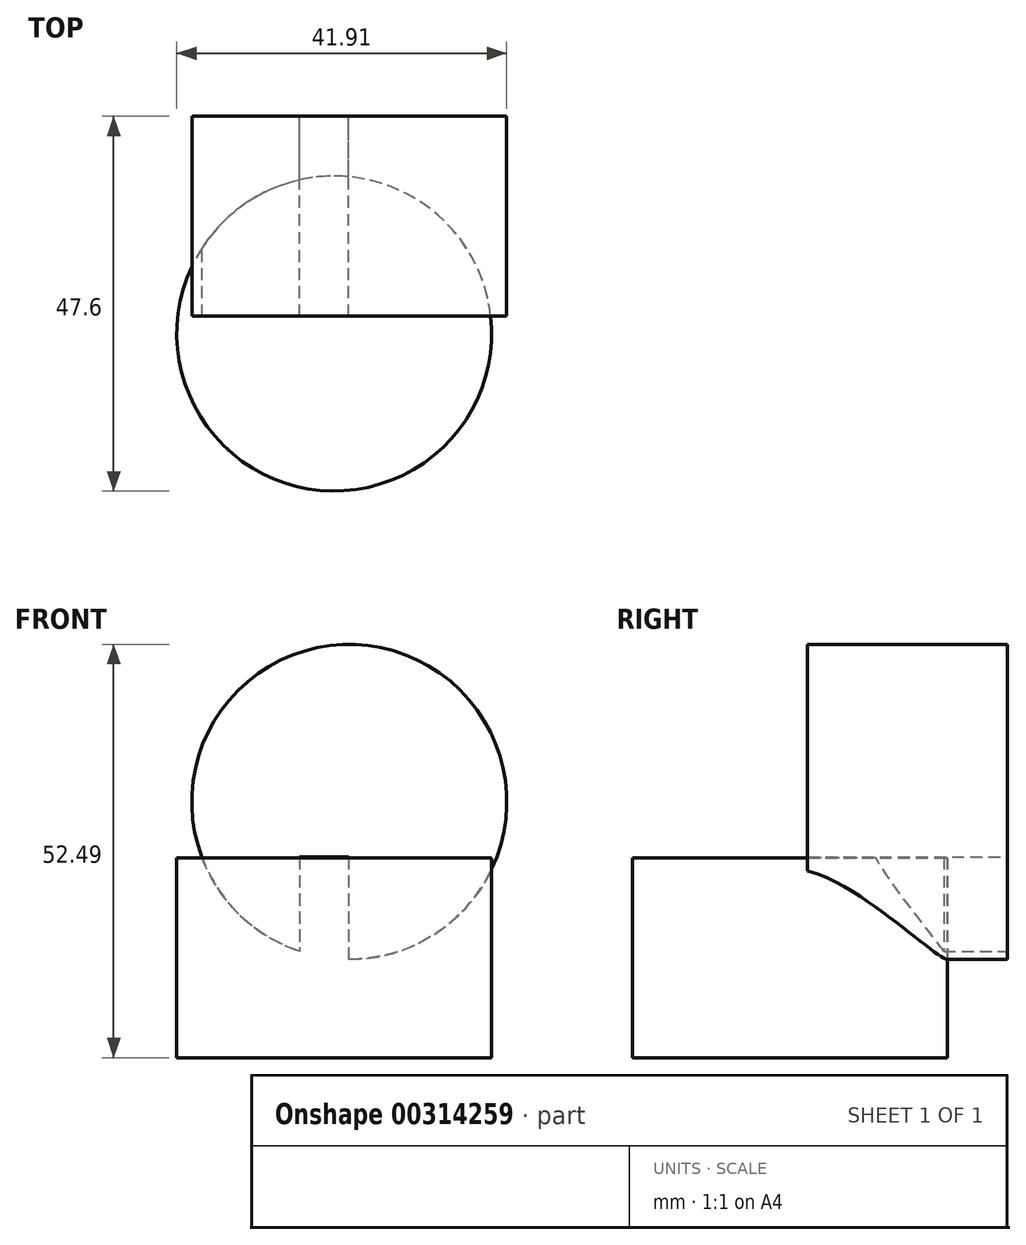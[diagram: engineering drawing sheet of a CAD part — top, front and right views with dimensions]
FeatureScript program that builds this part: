
annotation { "Feature Type Name" : "Feature", "Feature Type Description" : "" }
export const myFeature = defineFeature(function(context is Context, id is Id, definition is map)
    precondition{}
    {
        {
            var Q0;
            Q0=qCreatedBy(makeId("Top.planeOp"),FACE);
            var sketch = newSketch(context, id + "F0", { "sketchPlane" : qUnion([Q0])});
            skCircle(sketch, "E0", {"center": v(27.24, -27.6) * mm, "radius": 20 * mm});
            skSolve(sketch);
        }
        {
            var Q0;
            Q0 = qSketchRegion(id + "F0", true);
            extrude(context, id + "F1", {"entities" : qUnion([Q0]), "depth" : 25.4 * mm});
        }
        {
            var Q0;
            Q0=qCreatedBy(makeId("Front.planeOp"),FACE);
            var sketch = newSketch(context, id + "F2", { "sketchPlane" : qUnion([Q0])});
            skCircle(sketch, "E1", {"center": v(29.15, 32.49) * mm, "radius": 20 * mm});
            skLineSegment(sketch, "E2", {"start": v(7.15, 25.4) * mm, "end": v(7.15, 0) * mm});
            skLineSegment(sketch, "E3.bottom", {"start": v(22.84, 25.48) * mm, "end": v(29.07, 25.48) * mm});
            skLineSegment(sketch, "E3.top", {"start": v(22.84, 12.49) * mm, "end": v(29.07, 12.49) * mm});
            skLineSegment(sketch, "E3.left", {"start": v(22.84, 25.48) * mm, "end": v(22.84, 12.49) * mm});
            skLineSegment(sketch, "E3.right", {"start": v(29.07, 25.48) * mm, "end": v(29.07, 12.49) * mm});
            skSolve(sketch);
        }
        {
            var Q0;
            {var subQ4=sQuery(id+"F2.wireOp",EDGE,"E3.bottom");Q0=makeQuery(id+"F2.imprint","IMPRINT",FACE,{"disambiguationData":[TD([[makeQuery(id+"F2.imprint","IMPRINT",EDGE,{"derivedFrom":subQ4}),1.0]])]});}
            extrude(context, id + "F3", {"entities" : qUnion([Q0]), "operationType" : NewBodyOperationType.ADD, "depth" : 25.4 * mm});
        }
    });
